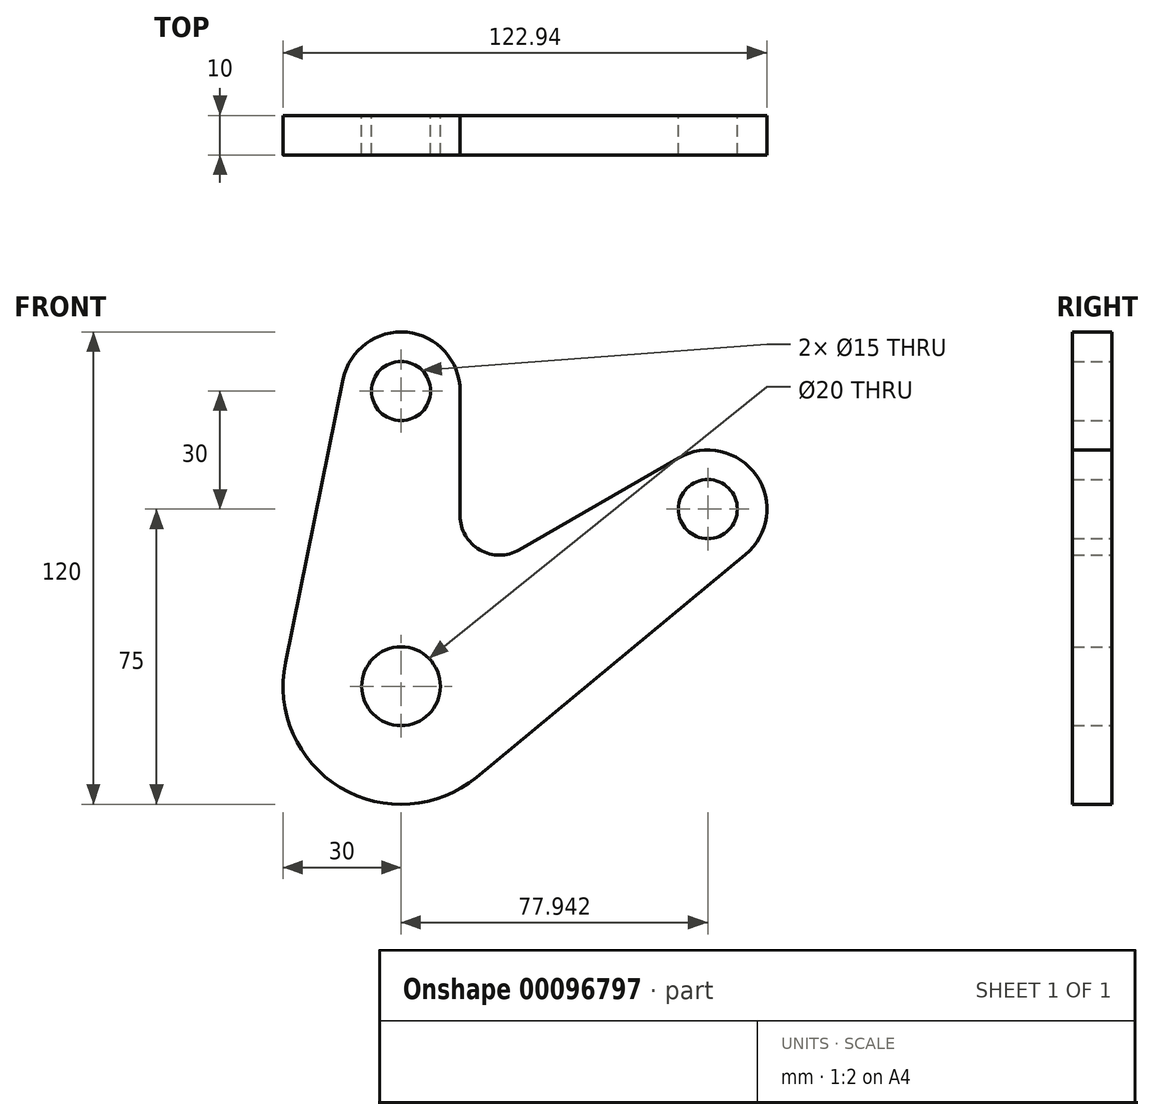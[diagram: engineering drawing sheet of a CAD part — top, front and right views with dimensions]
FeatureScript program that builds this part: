
annotation { "Feature Type Name" : "Feature", "Feature Type Description" : "" }
export const myFeature = defineFeature(function(context is Context, id is Id, definition is map)
    precondition{}
    {
        {
            var Q0;
            Q0=qCreatedBy(makeId("Front.planeOp"),FACE);
            var sketch = newSketch(context, id + "F0", { "sketchPlane" : qUnion([Q0])});
            skLineSegment(sketch, "E0", {"start": v(0, 82.89) * mm, "end": v(0, -40.83) * mm, "construction": true});
            skLineSegment(sketch, "E1", {"start": v(-7.6, 75) * mm, "end": v(7.5, 75) * mm, "construction": true});
            skLineSegment(sketch, "E2", {"start": v(-11.67, 0) * mm, "end": v(13.84, 0) * mm, "construction": true});
            skLineSegment(sketch, "E3", {"start": v(0, 0) * mm, "end": v(77.94, 45) * mm, "construction": true});
            skCircle(sketch, "E4", {"center": v(0, 75) * mm, "radius": 7.5 * mm});
            skCircle(sketch, "E5", {"center": v(0, 0) * mm, "radius": 10 * mm});
            skCircle(sketch, "E6", {"center": v(77.94, 45) * mm, "radius": 7.5 * mm});
            skLineSegment(sketch, "E7", {"start": v(70.44, 58) * mm, "end": v(30, 34.64) * mm});
            skArc(sketch, "E8", {"start": v(15, 43.3) * mm, "mid": v(20, 34.64) * mm, "end": v(30, 34.64) * mm});
            skLineSegment(sketch, "E9", {"start": v(-14.7, 78) * mm, "end": v(-29.4, 6) * mm});
            skArc(sketch, "E10", {"start": v(-14.7, 78) * mm, "mid": v(1.5, 89.92) * mm, "end": v(15, 75) * mm});
            skArc(sketch, "E11", {"start": v(-29.4, 6) * mm, "mid": v(-15.44, -25.72) * mm, "end": v(19.12, -23.12) * mm});
            skArc(sketch, "E12", {"start": v(70.44, 58) * mm, "mid": v(90.26, 53.56) * mm, "end": v(87.5, 33.44) * mm});
            skLineSegment(sketch, "E13", {"start": v(15, 75) * mm, "end": v(15, 43.3) * mm});
            skLineSegment(sketch, "E14", {"start": v(87.5, 33.44) * mm, "end": v(19.12, -23.12) * mm});
            skSolve(sketch);
        }
        {
            var Q0;
            Q0 = qSketchRegion(id + "F0", true);
            extrude(context, id + "F1", {"entities" : qUnion([Q0]), "depth" : 10 * mm});
        }
    });
